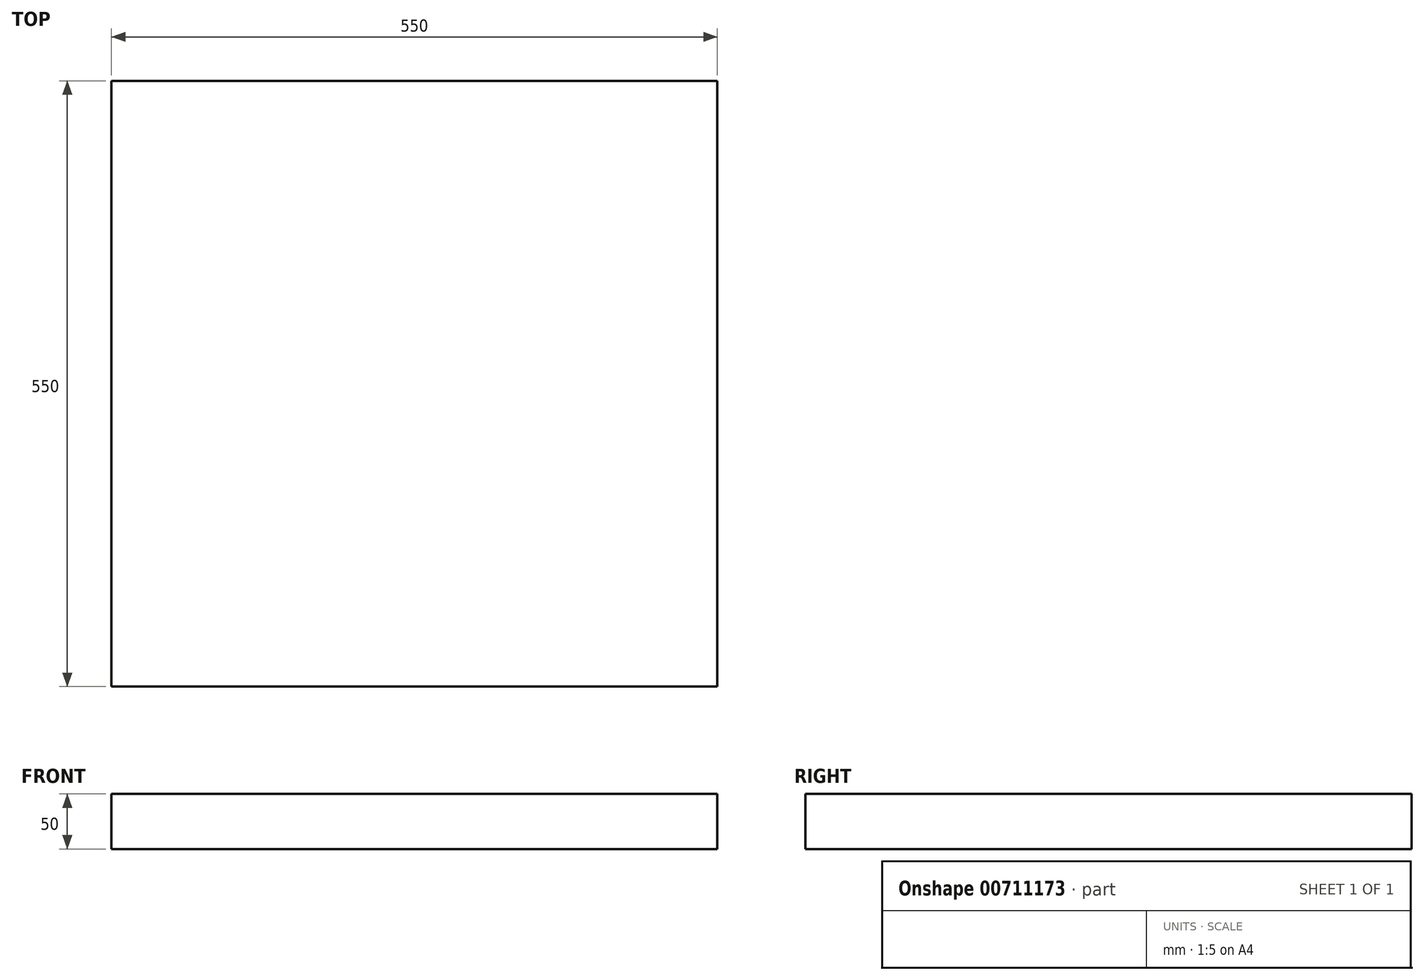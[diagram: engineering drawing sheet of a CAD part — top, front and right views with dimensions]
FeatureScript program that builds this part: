
annotation { "Feature Type Name" : "Feature", "Feature Type Description" : "" }
export const myFeature = defineFeature(function(context is Context, id is Id, definition is map)
    precondition{}
    {
        {
            var Q0;
            Q0=qCreatedBy(makeId("Top.planeOp"),FACE);
            var sketch = newSketch(context, id + "F0", { "sketchPlane" : qUnion([Q0])});
            skLineSegment(sketch, "E0.bottom", {"start": v(0, 0) * mm, "end": v(550, 0) * mm});
            skLineSegment(sketch, "E0.top", {"start": v(0, 550) * mm, "end": v(550, 550) * mm});
            skLineSegment(sketch, "E0.left", {"start": v(0, 0) * mm, "end": v(0, 550) * mm});
            skLineSegment(sketch, "E0.right", {"start": v(550, 0) * mm, "end": v(550, 550) * mm});
            skSolve(sketch);
        }
        {
            var Q0;
            Q0 = qSketchRegion(id + "F0", true);
            var Q1;
            Q1=makeQuery(id+"F0.imprint","IMPRINT",FACE,{"disambiguationData":[TD([[makeQuery(id+"F0.imprint","IMPRINT",EDGE,{"derivedFrom":sQuery(id+"F0.wireOp",EDGE,"E0.bottom")}),1.0]])]});
            extrude(context, id + "F1", {"entities" : qUnion([Q0, Q1]), "depth" : 50 * mm, "offsetDistance" : 25 * mm});
        }
    });
